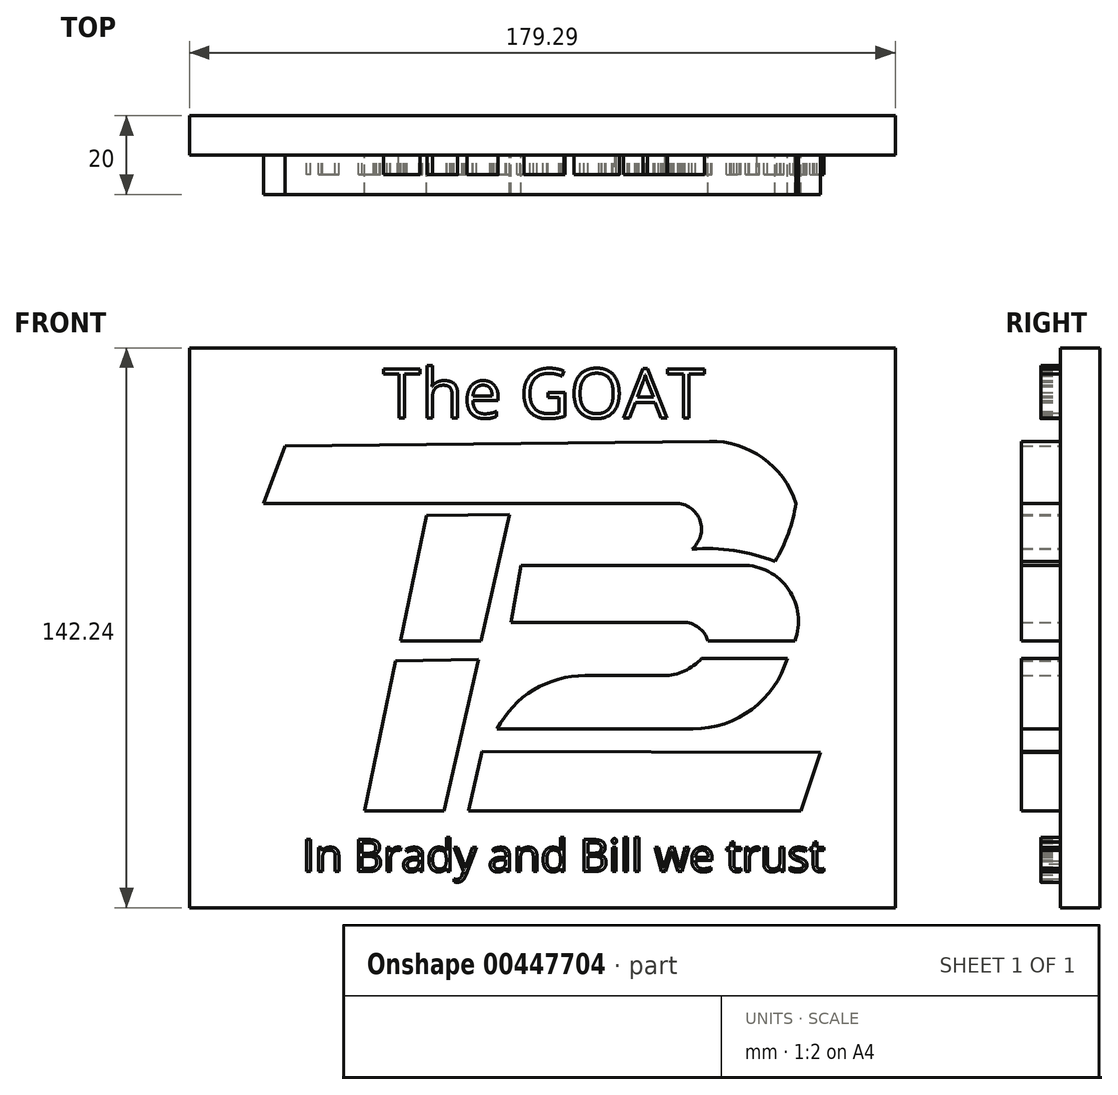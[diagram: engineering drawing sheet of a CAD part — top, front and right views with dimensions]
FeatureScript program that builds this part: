
annotation { "Feature Type Name" : "Feature", "Feature Type Description" : "" }
export const myFeature = defineFeature(function(context is Context, id is Id, definition is map)
    precondition{}
    {
        {
            var Q0;
            Q0=qCreatedBy(makeId("Front.planeOp"),FACE);
            var sketch = newSketch(context, id + "F0", { "sketchPlane" : qUnion([Q0])});
            skLineSegment(sketch, "E0.bottom", {"start": v(-87.44, 69.7) * mm, "end": v(91.85, 69.7) * mm});
            skLineSegment(sketch, "E0.top", {"start": v(-87.44, -72.54) * mm, "end": v(91.85, -72.54) * mm});
            skLineSegment(sketch, "E0.left", {"start": v(-87.44, 69.7) * mm, "end": v(-87.44, -72.54) * mm});
            skLineSegment(sketch, "E0.right", {"start": v(91.85, 69.7) * mm, "end": v(91.85, -72.54) * mm});
            skSolve(sketch);
        }
        {
            var Q0;
            Q0 = qSketchRegion(id + "F0", true);
            extrude(context, id + "F1", {"entities" : qUnion([Q0]), "depth" : 10 * mm});
        }
        {
            var Q0;
            Q0=makeQuery(id+"F1.opExtrude","CAP_FACE",FACE,{"disambiguationData":[OSD([sQuery(id+"F0.wireOp",EDGE,"E0.bottom"),sQuery(id+"F0.wireOp",EDGE,"E0.top"),sQuery(id+"F0.wireOp",EDGE,"E0.left"),sQuery(id+"F0.wireOp",EDGE,"E0.right")])],"isStart":false});
            var sketch = newSketch(context, id + "F2", { "sketchPlane" : qUnion([Q0])});
            skLineSegment(sketch, "E1", {"start": v(-68.64, 30.24) * mm, "end": v(36.07, 30.24) * mm});
            skLineSegment(sketch, "E2", {"start": v(-63.16, 44.73) * mm, "end": v(44.62, 45.99) * mm});
            skArc(sketch, "E3", {"start": v(40.16, 18.59) * mm, "mid": v(42.24, 25.86) * mm, "end": v(36.07, 30.24) * mm});
            skArc(sketch, "E4", {"start": v(66.62, 30.24) * mm, "mid": v(58.2, 41.72) * mm, "end": v(44.62, 45.99) * mm});
            skArc(sketch, "E5", {"start": v(61.27, 15.43) * mm, "mid": v(64.7, 22.56) * mm, "end": v(66.62, 30.24) * mm});
            skArc(sketch, "E6", {"start": v(61.27, 15.43) * mm, "mid": v(50.9, 18.2) * mm, "end": v(40.16, 18.59) * mm});
            skLineSegment(sketch, "E7", {"start": v(-68.64, 30.24) * mm, "end": v(-63.16, 44.73) * mm});
            skLineSegment(sketch, "E8", {"start": v(-27.25, 27.09) * mm, "end": v(-33.86, -4.73) * mm});
            skLineSegment(sketch, "E9", {"start": v(-27.25, 27.09) * mm, "end": v(-6.16, 27.34) * mm});
            skLineSegment(sketch, "E10", {"start": v(-6.16, 27.34) * mm, "end": v(-13.39, -4.73) * mm});
            skLineSegment(sketch, "E11", {"start": v(-13.39, -4.73) * mm, "end": v(-33.86, -4.73) * mm});
            skLineSegment(sketch, "E12", {"start": v(-35.12, -9.77) * mm, "end": v(-43, -47.88) * mm});
            skLineSegment(sketch, "E13", {"start": v(-43, -47.88) * mm, "end": v(-22.84, -47.88) * mm});
            skLineSegment(sketch, "E14", {"start": v(-22.84, -47.88) * mm, "end": v(-14.02, -9.45) * mm});
            skLineSegment(sketch, "E15", {"start": v(-14.02, -9.45) * mm, "end": v(-35.12, -9.77) * mm});
            skLineSegment(sketch, "E16", {"start": v(-3.27, 14.49) * mm, "end": v(-5.83, 0) * mm});
            skLineSegment(sketch, "E17", {"start": v(-5.83, 0) * mm, "end": v(37.96, 0) * mm});
            skLineSegment(sketch, "E18", {"start": v(-3.27, 14.49) * mm, "end": v(53.08, 14.49) * mm});
            skLineSegment(sketch, "E19", {"start": v(44.26, -4.73) * mm, "end": v(66.3, -4.73) * mm});
            skLineSegment(sketch, "E20", {"start": v(42.68, -9.13) * mm, "end": v(64.42, -9.13) * mm});
            skLineSegment(sketch, "E21", {"start": v(-9.3, -27.09) * mm, "end": v(40.48, -27.09) * mm});
            skLineSegment(sketch, "E22", {"start": v(-13.07, -32.76) * mm, "end": v(-16.54, -47.88) * mm});
            skLineSegment(sketch, "E23", {"start": v(-16.54, -47.88) * mm, "end": v(67.88, -47.88) * mm});
            skLineSegment(sketch, "E24", {"start": v(67.88, -47.88) * mm, "end": v(72.8, -33.08) * mm});
            skLineSegment(sketch, "E25", {"start": v(-13.07, -32.76) * mm, "end": v(72.8, -33.08) * mm});
            skArc(sketch, "E26", {"start": v(44.26, -4.73) * mm, "mid": v(41.9, -1.31) * mm, "end": v(37.96, 0) * mm});
            skArc(sketch, "E27", {"start": v(66.3, -4.73) * mm, "mid": v(64.74, 8.36) * mm, "end": v(53.08, 14.49) * mm});
            skArc(sketch, "E28", {"start": v(40.48, -27.09) * mm, "mid": v(55.44, -22.1) * mm, "end": v(64.42, -9.13) * mm});
            skLineSegment(sketch, "E29", {"start": v(13.07, -13.54) * mm, "end": v(32.92, -13.54) * mm});
            skArc(sketch, "E30", {"start": v(13.07, -13.54) * mm, "mid": v(0, -17.2) * mm, "end": v(-9.3, -27.09) * mm});
            skArc(sketch, "E31", {"start": v(32.92, -13.54) * mm, "mid": v(38.27, -12.4) * mm, "end": v(42.68, -9.13) * mm});
            skSolve(sketch);
        }
        {
            var Q0;
            Q0 = qSketchRegion(id + "F2", true);
            extrude(context, id + "F3", {"entities" : qUnion([Q0]), "operationType" : NewBodyOperationType.ADD, "depth" : 10 * mm});
        }
        {
            var Q0;
            Q0=makeQuery(id+"F1.opExtrude","CAP_FACE",FACE,{"disambiguationData":[OSD([sQuery(id+"F0.wireOp",EDGE,"E0.bottom"),sQuery(id+"F0.wireOp",EDGE,"E0.top"),sQuery(id+"F0.wireOp",EDGE,"E0.left"),sQuery(id+"F0.wireOp",EDGE,"E0.right")])],"isStart":false});
            var sketch = newSketch(context, id + "F4", { "sketchPlane" : qUnion([Q0])});
            skText(sketch, "E32", { "text": "The GOAT\n", "fontName": "OpenSans-Regular.ttf"});
            skText(sketch, "E33", { "text": "In Brady and Bill we trust", "fontName": "OpenSans-Regular.ttf"});
            const initialGuessF4  = {"E32": [-0.03835, 0.05189, 1, 0, 0.0126], "E33": [-0.05876, -0.06332, 1, 0, 0.0082]};
            skSetInitialGuess(sketch, initialGuessF4);
            skSolve(sketch);
        }
        {
            var Q0;
            Q0 = qSketchRegion(id + "F4", true);
            extrude(context, id + "F5", {"entities" : qUnion([Q0]), "operationType" : NewBodyOperationType.ADD, "depth" : 5 * mm});
        }
    });
